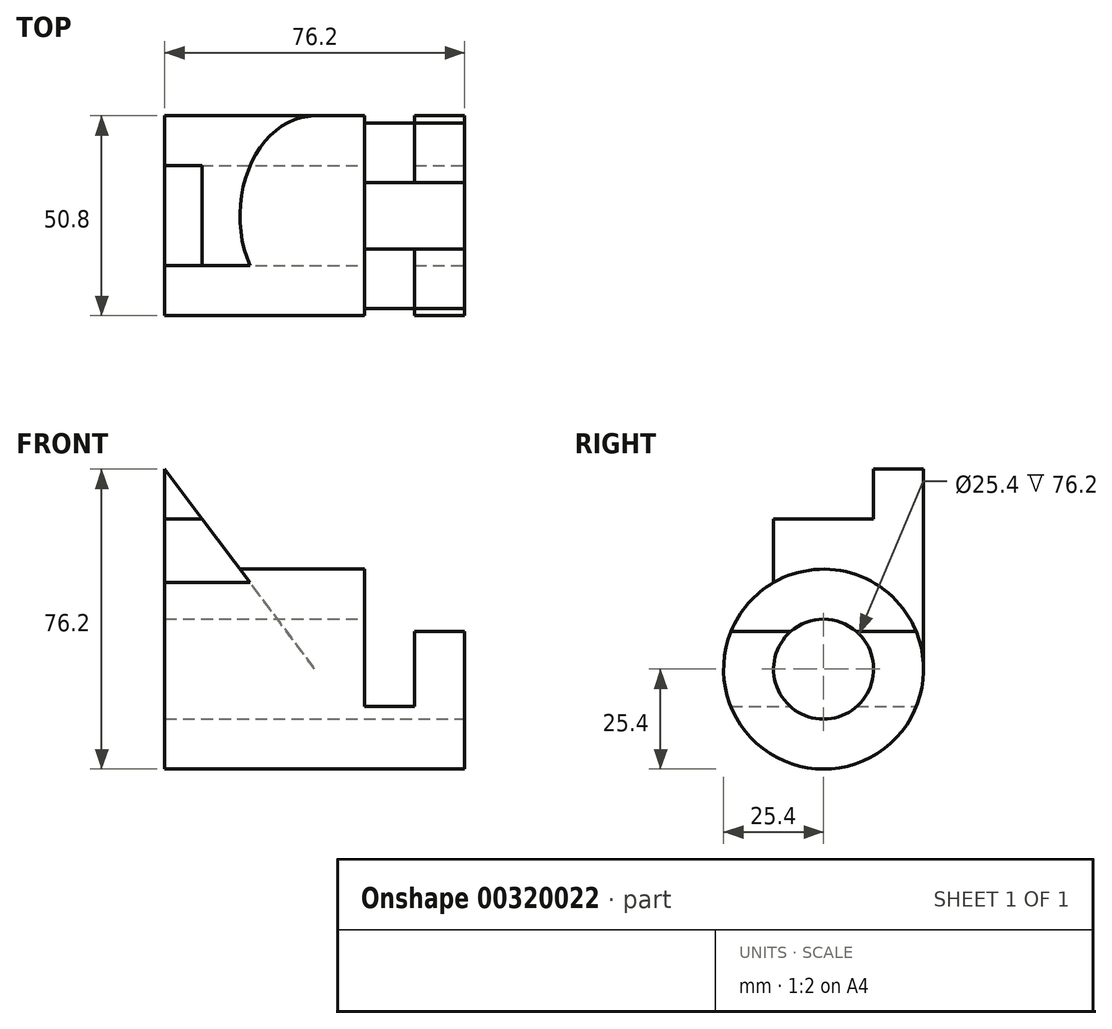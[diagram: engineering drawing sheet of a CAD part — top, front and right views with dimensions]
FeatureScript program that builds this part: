
annotation { "Feature Type Name" : "Feature", "Feature Type Description" : "" }
export const myFeature = defineFeature(function(context is Context, id is Id, definition is map)
    precondition{}
    {
        {
            var Q0;
            Q0=qCreatedBy(makeId("Right.planeOp"),FACE);
            var sketch = newSketch(context, id + "F0", { "sketchPlane" : qUnion([Q0])});
            skCircle(sketch, "E0", {"center": v(0, 0) * mm, "radius": 12.7 * mm});
            skCircle(sketch, "E1", {"center": v(0, 0) * mm, "radius": 25.4 * mm});
            skSolve(sketch);
        }
        {
            var Q0;
            Q0 = qSketchRegion(id + "F0", true);
            extrude(context, id + "F1", {"entities" : qUnion([Q0]), "depth" : 76.2 * mm});
        }
        {
            var Q0;
            Q0=qCreatedBy(makeId("Front.planeOp"),FACE);
            var sketch = newSketch(context, id + "F2", { "sketchPlane" : qUnion([Q0])});
            skLineSegment(sketch, "E2", {"start": v(76.2, 0) * mm, "end": v(76.2, 50.8) * mm});
            skLineSegment(sketch, "E3", {"start": v(76.2, 50.8) * mm, "end": v(38.1, 0) * mm});
            skLineSegment(sketch, "E4", {"start": v(38.1, 0) * mm, "end": v(76.2, 0) * mm});
            skSolve(sketch);
        }
        {
            var Q0;
            Q0 = qSketchRegion(id + "F2", true);
            extrude(context, id + "F3", {"entities" : qUnion([Q0]), "operationType" : NewBodyOperationType.ADD, "oppositeDirection" : true, "depth" : 12.7 * mm, "hasSecondDirection" : true, "secondDirectionOppositeDirection" : false, "secondDirectionDepth" : 25.4 * mm});
        }
        {
            var Q0;
            Q0=makeQuery(id+"F3.opExtrude","CAP_FACE",FACE,{"disambiguationData":[OSD([sQuery(id+"F2.wireOp",EDGE,"E2"),sQuery(id+"F2.wireOp",EDGE,"E3"),sQuery(id+"F2.wireOp",EDGE,"E4")])],"isStart":false});
            var sketch = newSketch(context, id + "F4", { "sketchPlane" : qUnion([Q0])});
            skLineSegment(sketch, "E5", {"start": v(-76.2, 50.8) * mm, "end": v(-76.2, 38.1) * mm});
            skLineSegment(sketch, "E6", {"start": v(-76.2, 38.1) * mm, "end": v(-66.68, 38.1) * mm});
            skLineSegment(sketch, "E7", {"start": v(-66.68, 38.1) * mm, "end": v(-76.2, 50.8) * mm});
            skSolve(sketch);
        }
        {
            var Q0;
            Q0 = qSketchRegion(id + "F4", true);
            extrude(context, id + "F5", {"entities" : qUnion([Q0]), "operationType" : NewBodyOperationType.REMOVE, "oppositeDirection" : true, "depth" : 25.4 * mm});
        }
        {
            var Q0;
            Q0=makeQuery(id+"F1.opExtrude","CAP_FACE",FACE,{"disambiguationData":[OSD([sQuery(id+"F0.wireOp",EDGE,"E0"),sQuery(id+"F0.wireOp",EDGE,"E1")])],"isStart":true});
            var sketch = newSketch(context, id + "F6", { "sketchPlane" : qUnion([Q0])});
            skCircle(sketch, "E8", {"center": v(0, 0) * mm, "radius": 12.7 * mm});
            skSolve(sketch);
        }
        {
            var Q0;
            Q0 = qSketchRegion(id + "F6", true);
            extrude(context, id + "F7", {"entities" : qUnion([Q0]), "operationType" : NewBodyOperationType.REMOVE, "endBound" : BoundingType.THROUGH_ALL, "oppositeDirection" : true, "depth" : 25.4 * mm});
        }
        {
            var Q0;
            Q0=qCreatedBy(makeId("Front.planeOp"),FACE);
            var sketch = newSketch(context, id + "F8", { "sketchPlane" : qUnion([Q0])});
            skLineSegment(sketch, "E9", {"start": v(25.4, 0) * mm, "end": v(25.4, 25.4) * mm});
            skLineSegment(sketch, "E10", {"start": v(25.4, 25.4) * mm, "end": v(0, 25.4) * mm});
            skLineSegment(sketch, "E11", {"start": v(0, 25.4) * mm, "end": v(0, 9.52) * mm});
            skLineSegment(sketch, "E12", {"start": v(0, 9.52) * mm, "end": v(12.7, 9.53) * mm});
            skLineSegment(sketch, "E13", {"start": v(12.7, 9.53) * mm, "end": v(12.7, 0) * mm});
            skLineSegment(sketch, "E14", {"start": v(12.7, 0) * mm, "end": v(12.7, -9.52) * mm});
            skLineSegment(sketch, "E15", {"start": v(12.7, -9.52) * mm, "end": v(25.4, -9.52) * mm});
            skLineSegment(sketch, "E16", {"start": v(25.4, -9.52) * mm, "end": v(25.4, 0) * mm});
            skSolve(sketch);
        }
        {
            var Q0;
            Q0 = qSketchRegion(id + "F8", true);
            extrude(context, id + "F9", {"entities" : qUnion([Q0]), "operationType" : NewBodyOperationType.REMOVE, "endBound" : BoundingType.THROUGH_ALL, "oppositeDirection" : true, "depth" : 25.4 * mm, "hasSecondDirection" : true, "secondDirectionBound" : SecondDirectionBoundingType.THROUGH_ALL, "secondDirectionOppositeDirection" : false, "secondDirectionDepth" : 25.4 * mm});
        }
        {
            var Q0;
            Q0=qCreatedBy(makeId("Right.planeOp"),FACE);
            var sketch = newSketch(context, id + "F10", { "sketchPlane" : qUnion([Q0])});
            skLineSegment(sketch, "E17", {"start": v(0, 0) * mm, "end": v(0, 57.71) * mm, "construction": true});
            skSolve(sketch);
        }
        {
            var Q0;
            Q0=makeQuery(id+"F1.opExtrude","SWEPT_BODY",BODY,{"disambiguationData":[OSD([sQuery(id+"F0.wireOp",EDGE,"E0"),sQuery(id+"F0.wireOp",EDGE,"E1")])]});
            var Q1;
            Q1=sQuery(id+"F10.wireOp",EDGE,"E17");
            transform(context, id + "F11", {"entities" : qUnion([Q0]), "transformType" : TransformType.ROTATION, "transformAxis" : qUnion([Q1]), "angle" : 180 * degree, "makeCopy" : false});
        }
    });
